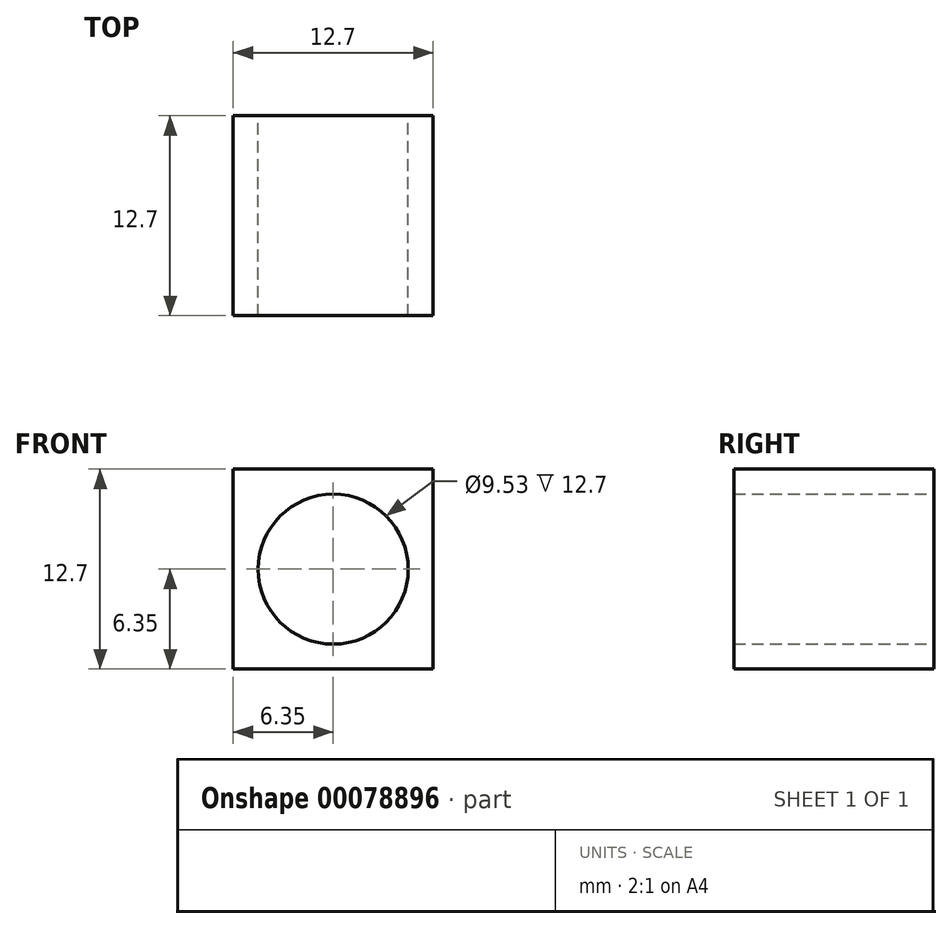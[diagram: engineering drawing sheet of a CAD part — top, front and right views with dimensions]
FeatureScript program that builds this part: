
annotation { "Feature Type Name" : "Feature", "Feature Type Description" : "" }
export const myFeature = defineFeature(function(context is Context, id is Id, definition is map)
    precondition{}
    {
        {
            var Q0;
            Q0=qCreatedBy(makeId("Front.planeOp"),FACE);
            var sketch = newSketch(context, id + "F0", { "sketchPlane" : qUnion([Q0])});
            skLineSegment(sketch, "E0.bottom", {"start": v(6.35, -6.35) * mm, "end": v(-6.35, -6.35) * mm});
            skLineSegment(sketch, "E0.top", {"start": v(6.35, 6.35) * mm, "end": v(-6.35, 6.35) * mm});
            skLineSegment(sketch, "E0.left", {"start": v(6.35, -6.35) * mm, "end": v(6.35, 6.35) * mm});
            skLineSegment(sketch, "E0.right", {"start": v(-6.35, -6.35) * mm, "end": v(-6.35, 6.35) * mm});
            skPoint(sketch, "E0.middle", {"position": v(0, 0) * mm});
            skCircle(sketch, "E1", {"center": v(0, 0) * mm, "radius": 4.76 * mm});
            skSolve(sketch);
        }
        {
            var Q0;
            Q0 = qSketchRegion(id + "F0", true);
            extrude(context, id + "F1", {"entities" : qUnion([Q0]), "depth" : 12.7 * mm});
        }
    });
